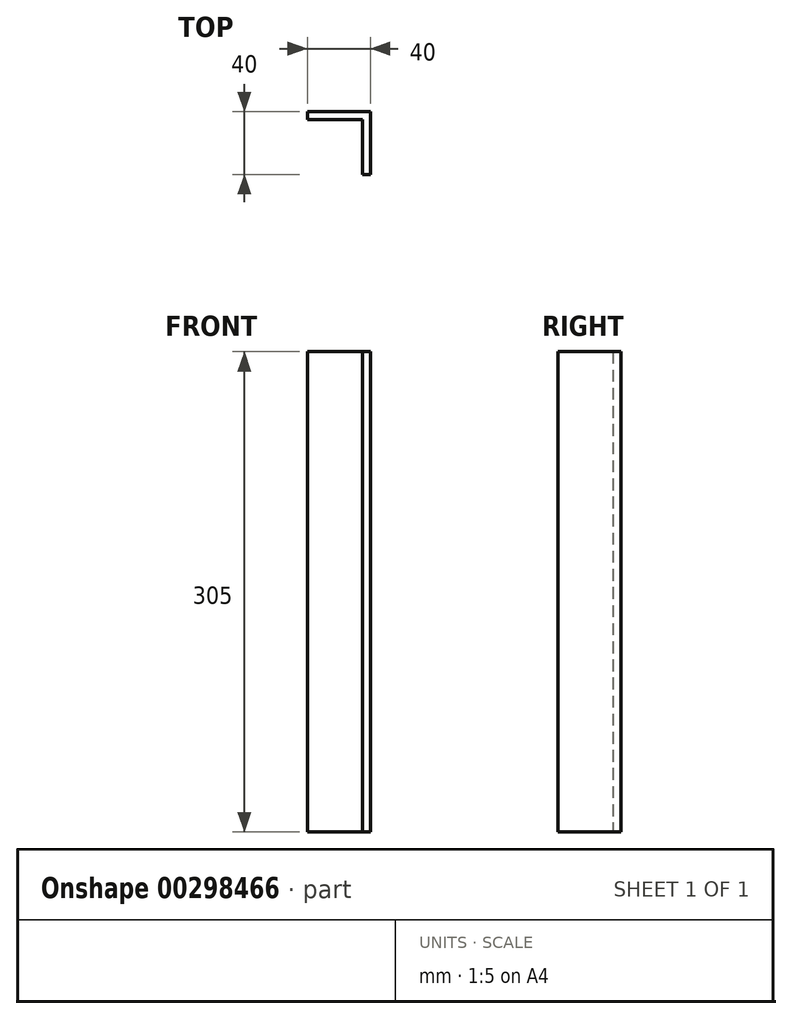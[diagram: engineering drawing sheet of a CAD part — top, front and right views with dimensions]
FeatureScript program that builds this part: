
annotation { "Feature Type Name" : "Feature", "Feature Type Description" : "" }
export const myFeature = defineFeature(function(context is Context, id is Id, definition is map)
    precondition{}
    {
        {
            var Q0;
            Q0=qCreatedBy(makeId("Top.planeOp"),FACE);
            var sketch = newSketch(context, id + "F0", { "sketchPlane" : qUnion([Q0])});
            skLineSegment(sketch, "E0.bottom", {"start": v(20, 20) * mm, "end": v(-20, 20) * mm});
            skLineSegment(sketch, "E0.top", {"start": v(20, -20) * mm, "end": v(15, -20) * mm});
            skLineSegment(sketch, "E0.left", {"start": v(20, 20) * mm, "end": v(20, -20) * mm});
            skLineSegment(sketch, "E0.right", {"start": v(-20, 20) * mm, "end": v(-20, 15) * mm});
            skPoint(sketch, "E0.middle", {"position": v(0, 0) * mm});
            skLineSegment(sketch, "E1.0", {"start": v(15, 15) * mm, "end": v(-20, 15) * mm});
            skLineSegment(sketch, "E1.1", {"start": v(15, 15) * mm, "end": v(15, -20) * mm});
            skPoint(sketch, "E2.orphan", {"position": v(-20, -20) * mm});
            skSolve(sketch);
        }
        {
            var Q0;
            Q0 = qSketchRegion(id + "F0", true);
            extrude(context, id + "F1", {"entities" : qUnion([Q0]), "depth" : 305 * mm});
        }
        {
            var Q0;
            Q0=makeQuery(id+"F1.opExtrude","SWEPT_FACE",FACE,{"disambiguationData":[OSD([sQuery(id+"F0.wireOp",EDGE,"E0.left")])]});
            var sketch = newSketch(context, id + "F2", { "sketchPlane" : qUnion([Q0])});
            skLineSegment(sketch, "E3.bottom", {"start": v(-20, 20) * mm, "end": v(20, 20) * mm});
            skLineSegment(sketch, "E3.top", {"start": v(-20, 60) * mm, "end": v(20, 60) * mm});
            skLineSegment(sketch, "E3.left", {"start": v(-20, 20) * mm, "end": v(-20, 60) * mm});
            skLineSegment(sketch, "E3.right", {"start": v(20, 20) * mm, "end": v(20, 60) * mm});
            skLineSegment(sketch, "E4.0.1.0", {"start": v(-20, 245) * mm, "end": v(20, 245) * mm});
            skLineSegment(sketch, "E4.0.1.1", {"start": v(-20, 285) * mm, "end": v(20, 285) * mm});
            skLineSegment(sketch, "E4.direction1", {"start": v(-20, 20) * mm, "end": v(5, 20) * mm, "construction": true});
            skLineSegment(sketch, "E4.direction2", {"start": v(-20, 20) * mm, "end": v(-20, 245) * mm, "construction": true});
            skSolve(sketch);
        }
        {
            var Q0;
            Q0=makeQuery(id+"F1.opExtrude","SWEPT_FACE",FACE,{"disambiguationData":[OSD([sQuery(id+"F0.wireOp",EDGE,"E0.bottom")])]});
            var sketch = newSketch(context, id + "F3", { "sketchPlane" : qUnion([Q0])});
            skLineSegment(sketch, "E5.bottom", {"start": v(-20, 20) * mm, "end": v(20, 20) * mm});
            skLineSegment(sketch, "E5.top", {"start": v(-20, 60) * mm, "end": v(20, 60) * mm});
            skLineSegment(sketch, "E5.left", {"start": v(-20, 20) * mm, "end": v(-20, 60) * mm});
            skLineSegment(sketch, "E5.right", {"start": v(20, 20) * mm, "end": v(20, 60) * mm});
            skLineSegment(sketch, "E6.0.1.0", {"start": v(-20, 285) * mm, "end": v(20, 285) * mm});
            skLineSegment(sketch, "E6.0.1.1", {"start": v(-20, 245) * mm, "end": v(20, 245) * mm});
            skLineSegment(sketch, "E6.direction1", {"start": v(-20, 60) * mm, "end": v(5, 60) * mm, "construction": true});
            skLineSegment(sketch, "E6.direction2", {"start": v(-20, 60) * mm, "end": v(-20, 285) * mm, "construction": true});
            skSolve(sketch);
        }
    });
